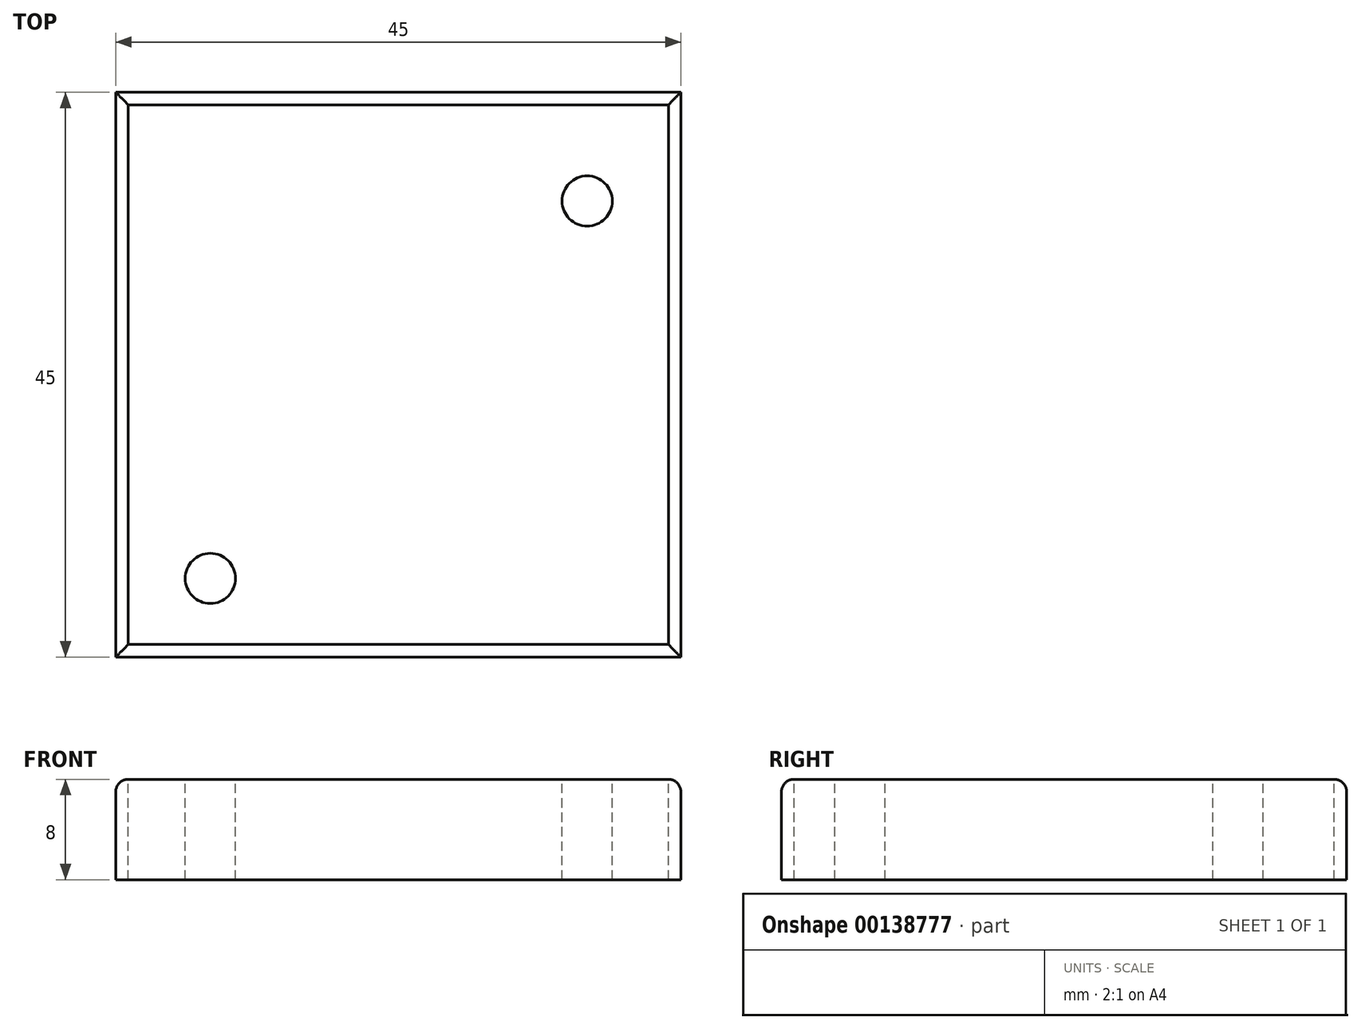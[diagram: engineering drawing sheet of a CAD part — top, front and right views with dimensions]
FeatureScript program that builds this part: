
annotation { "Feature Type Name" : "Feature", "Feature Type Description" : "" }
export const myFeature = defineFeature(function(context is Context, id is Id, definition is map)
    precondition{}
    {
        {
            var Q0;
            Q0=qCreatedBy(makeId("Top.planeOp"),FACE);
            var sketch = newSketch(context, id + "F0", { "sketchPlane" : qUnion([Q0])});
            skLineSegment(sketch, "E0.bottom", {"start": v(-22.64, 23.74) * mm, "end": v(22.36, 23.74) * mm});
            skLineSegment(sketch, "E0.top", {"start": v(-22.64, -21.26) * mm, "end": v(22.36, -21.26) * mm});
            skLineSegment(sketch, "E0.left", {"start": v(-22.64, 23.74) * mm, "end": v(-22.64, -21.26) * mm});
            skLineSegment(sketch, "E0.right", {"start": v(22.36, 23.74) * mm, "end": v(22.36, -21.26) * mm});
            skSolve(sketch);
        }
        {
            var Q0;
            Q0=makeQuery(id+"F0.imprint","IMPRINT",FACE,{"disambiguationData":[TD([[makeQuery(id+"F0.imprint","IMPRINT",EDGE,{"derivedFrom":sQuery(id+"F0.wireOp",EDGE,"E0.bottom")}),-1.0]])]});
            extrude(context, id + "F1", {"entities" : qUnion([Q0]), "depth" : 8 * mm});
        }
        {
            var Q0;
            Q0=makeQuery(id+"F1.opExtrude","CAP_FACE",FACE,{"disambiguationData":[OSD([sQuery(id+"F0.wireOp",EDGE,"E0.bottom"),sQuery(id+"F0.wireOp",EDGE,"E0.top"),sQuery(id+"F0.wireOp",EDGE,"E0.left"),sQuery(id+"F0.wireOp",EDGE,"E0.right")])],"isStart":false});
            var sketch = newSketch(context, id + "F2", { "sketchPlane" : qUnion([Q0])});
            skCircle(sketch, "E1", {"center": v(0, 0) * mm, "radius": 14.25 * mm});
            skCircle(sketch, "E2", {"center": v(0, 0) * mm, "radius": 15.5 * mm});
            skSolve(sketch);
        }
        {
            var Q0;
            Q0=makeQuery(id+"F2.imprint","IMPRINT",FACE,{"disambiguationData":[TD([[makeQuery(id+"F2.imprint","IMPRINT",EDGE,{"derivedFrom":sQuery(id+"F2.wireOp",EDGE,"E1")}),1.0]])]});
            extrude(context, id + "F3", {"entities" : qUnion([Q0]), "operationType" : NewBodyOperationType.REMOVE, "endBound" : BoundingType.THROUGH_ALL, "depth" : 5 * mm, "hasSecondDirection" : true, "secondDirectionOppositeDirection" : true, "secondDirectionDepth" : 8 * mm});
        }
        {
            var Q0;
            Q0=makeQuery(id+"F1.opExtrude","CAP_FACE",FACE,{"disambiguationData":[OSD([sQuery(id+"F0.wireOp",EDGE,"E0.bottom"),sQuery(id+"F0.wireOp",EDGE,"E0.top"),sQuery(id+"F0.wireOp",EDGE,"E0.left"),sQuery(id+"F0.wireOp",EDGE,"E0.right")])],"isStart":false});
            var sketch = newSketch(context, id + "F4", { "sketchPlane" : qUnion([Q0])});
            skCircle(sketch, "E3", {"center": v(0, 0) * mm, "radius": 15.5 * mm});
            skSolve(sketch);
        }
        {
            var Q0;
            Q0=makeQuery(id+"F4.imprint","IMPRINT",FACE,{"disambiguationData":[TD([[makeQuery(id+"F4.imprint","IMPRINT",EDGE,{"derivedFrom":sQuery(id+"F4.wireOp",EDGE,"E3")}),-1.0]])]});
            var Q1;
            Q1=sQuery(id+"F4.wireOp",EDGE,"E3");
            extrude(context, id + "F5", {"entities" : qUnion([Q0]), "operationType" : NewBodyOperationType.REMOVE, "surfaceEntities" : qUnion([Q1]), "depth" : 1.5 * mm});
        }
        {
            var Q0;
            Q0=makeQuery(id+"F1.opExtrude","CAP_EDGE",EDGE,{"disambiguationData":[OSD([sQuery(id+"F0.wireOp",EDGE,"E0.bottom")])],"isStart":false});
            var Q1;
            Q1=makeQuery(id+"F1.opExtrude","CAP_EDGE",EDGE,{"disambiguationData":[OSD([sQuery(id+"F0.wireOp",EDGE,"E0.left")])],"isStart":false});
            var Q2;
            Q2=makeQuery(id+"F1.opExtrude","CAP_EDGE",EDGE,{"disambiguationData":[OSD([sQuery(id+"F0.wireOp",EDGE,"E0.top")])],"isStart":false});
            var Q3;
            Q3=makeQuery(id+"F1.opExtrude","CAP_EDGE",EDGE,{"disambiguationData":[OSD([sQuery(id+"F0.wireOp",EDGE,"E0.right")])],"isStart":false});
            fillet(context, id + "F6", {"entities" : qUnion([Q0, Q1, Q2, Q3]), "radius" : 1 * mm, "tangentPropagation" : true, "allowEdgeOverflow" : false});
        }
        {
            var Q0;
            Q0=makeQuery(id+"F1.opExtrude","CAP_FACE",FACE,{"disambiguationData":[OSD([sQuery(id+"F0.wireOp",EDGE,"E0.bottom"),sQuery(id+"F0.wireOp",EDGE,"E0.top"),sQuery(id+"F0.wireOp",EDGE,"E0.left"),sQuery(id+"F0.wireOp",EDGE,"E0.right")])],"isStart":false});
            var sketch = newSketch(context, id + "F7", { "sketchPlane" : qUnion([Q0])});
            skCircle(sketch, "E4", {"center": v(-15.1, 15) * mm, "radius": 2 * mm});
            skCircle(sketch, "E5.MirrorC", {"center": v(-15.1, -15) * mm, "radius": 2 * mm});
            skLineSegment(sketch, "E6", {"start": v(-0.14, 29.57) * mm, "end": v(0, -28.25) * mm});
            skPoint(sketch, "E6.startSnap0", {"position": v(-0.14, 22.74) * mm});
            skCircle(sketch, "E7.MirrorC", {"center": v(14.9, 15.08) * mm, "radius": 2 * mm});
            skCircle(sketch, "E8.MirrorC", {"center": v(15.04, -14.92) * mm, "radius": 2 * mm});
            skSolve(sketch);
        }
        {
            var Q0;
            Q0=makeQuery(id+"F7.imprint","IMPRINT",FACE,{"disambiguationData":[TD([[makeQuery(id+"F7.imprint","IMPRINT",EDGE,{"derivedFrom":sQuery(id+"F7.wireOp",EDGE,"E4")}),1.0]])]});
            var Q1;
            Q1=makeQuery(id+"F7.imprint","IMPRINT",FACE,{"disambiguationData":[TD([[makeQuery(id+"F7.imprint","IMPRINT",EDGE,{"derivedFrom":sQuery(id+"F7.wireOp",EDGE,"E7.MirrorC")}),-1.0]])]});
            var Q2;
            Q2=makeQuery(id+"F7.imprint","IMPRINT",FACE,{"disambiguationData":[TD([[makeQuery(id+"F7.imprint","IMPRINT",EDGE,{"derivedFrom":sQuery(id+"F7.wireOp",EDGE,"E8.MirrorC")}),1.0]])]});
            var Q3;
            Q3=makeQuery(id+"F7.imprint","IMPRINT",FACE,{"disambiguationData":[TD([[makeQuery(id+"F7.imprint","IMPRINT",EDGE,{"derivedFrom":sQuery(id+"F7.wireOp",EDGE,"E5.MirrorC")}),-1.0]])]});
            var Q4;
            Q4=sQuery(id+"F7.wireOp",EDGE,"E4");
            var Q5;
            Q5=sQuery(id+"F7.wireOp",EDGE,"E7.MirrorC");
            var Q6;
            Q6=sQuery(id+"F7.wireOp",EDGE,"E8.MirrorC");
            var Q7;
            Q7=sQuery(id+"F7.wireOp",EDGE,"E5.MirrorC");
            extrude(context, id + "F8", {"entities" : qUnion([Q0, Q1, Q2, Q3]), "operationType" : NewBodyOperationType.REMOVE, "surfaceEntities" : qUnion([Q4, Q5, Q6, Q7]), "oppositeDirection" : true, "depth" : 8 * mm});
        }
        {
            var Q0;
            Q0 = qSketchRegion(id + "F4", true);
            extrude(context, id + "F9", {"entities" : qUnion([Q0]), "operationType" : NewBodyOperationType.REMOVE, "oppositeDirection" : true, "depth" : 1.5 * mm});
        }
    });
